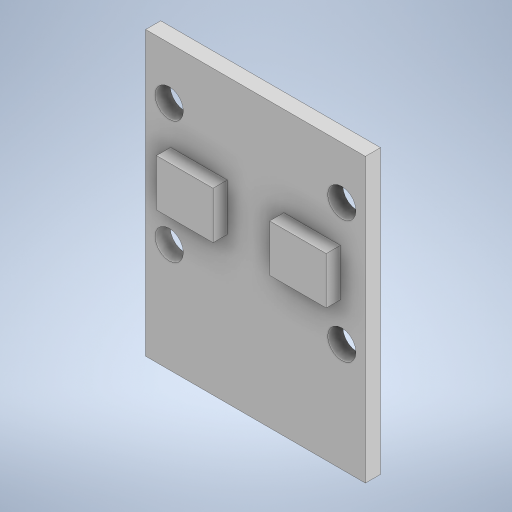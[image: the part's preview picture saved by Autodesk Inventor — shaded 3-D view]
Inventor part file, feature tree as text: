
AUTODESK INVENTOR PART (.ipt)
format: ipt  version: 2023.1 (Build 271208000, 208)  size: 253,440 bytes
history: native  units: mm
features: extrude x2, sketch x2, other x1
ambient origin geometry x8: Origin, YZ Plane, XZ Plane, XY Plane, X Axis, Y Axis, Z Axis, Center Point
bodies: Body1 (feature_tree)
feature tree (5):
  other  "솔리드1"
  extrude  "돌출1"  Depth=23.3mm
  extrude  "돌출2"  Depth=30.0mm
  sketch  "스케치1"
  sketch  "스케치2"
